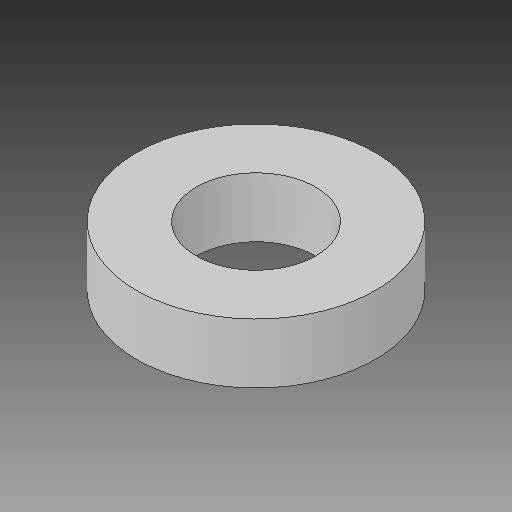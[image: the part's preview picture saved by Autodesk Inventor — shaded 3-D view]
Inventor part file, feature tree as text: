
AUTODESK INVENTOR PART (.ipt)
format: ipt  version: 2017 (Build 210142000, 142)  size: 95,744 bytes
history: native  units: in
note: dims shown in document units (in); Inventor stores cm internally (conversion verified against a paired STEP export)
features: extrude x1, sketch x1
ambient origin geometry x8: Origin, YZ Plane, XZ Plane, XY Plane, X Axis, Y Axis, Z Axis, Center Point
bodies: Solid1 (feature_tree)
feature tree (2):
  extrude  "Extrusion1"  Depth=0.125in
  sketch  "Sketch1"  dims[d0=0.25in d1=0.5in d2=0.125in d3=0.0in]
